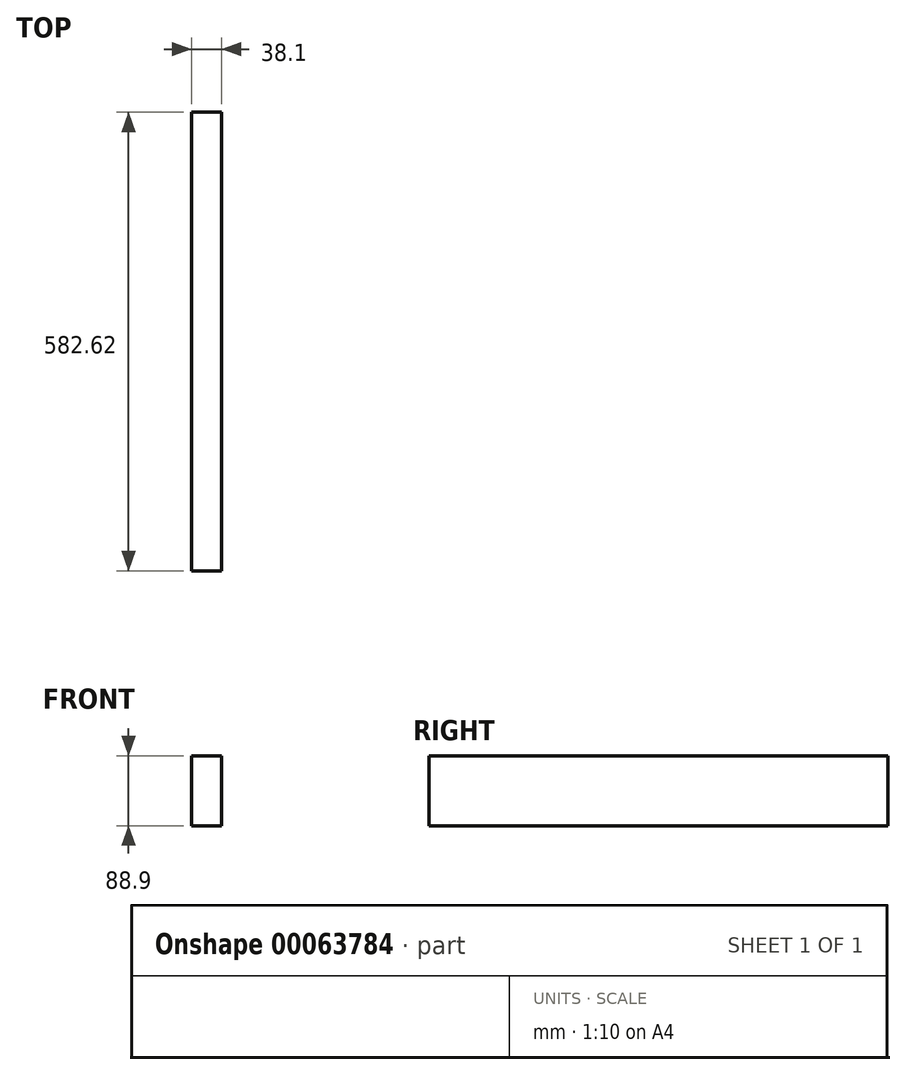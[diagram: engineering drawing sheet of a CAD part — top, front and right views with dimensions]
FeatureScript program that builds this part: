
annotation { "Feature Type Name" : "Feature", "Feature Type Description" : "" }
export const myFeature = defineFeature(function(context is Context, id is Id, definition is map)
    precondition{}
    {
        {
            var Q0;
            Q0=qCreatedBy(makeId("Front.planeOp"),FACE);
            var sketch = newSketch(context, id + "F0", { "sketchPlane" : qUnion([Q0])});
            skLineSegment(sketch, "E0.bottom", {"start": v(-18, 55.77) * mm, "end": v(20.1, 55.77) * mm});
            skLineSegment(sketch, "E0.top", {"start": v(-18, -33.13) * mm, "end": v(20.1, -33.13) * mm});
            skLineSegment(sketch, "E0.left", {"start": v(-18, 55.77) * mm, "end": v(-18, -33.13) * mm});
            skLineSegment(sketch, "E0.right", {"start": v(20.1, 55.77) * mm, "end": v(20.1, -33.13) * mm});
            skSolve(sketch);
        }
        {
            var Q0;
            Q0=qSketchRegion(id+"F0",true);
            extrude(context, id + "F1", {"entities" : qUnion([Q0]), "endBound" : BoundingType.SYMMETRIC, "depth" : 582.6 * mm});
        }
    });
